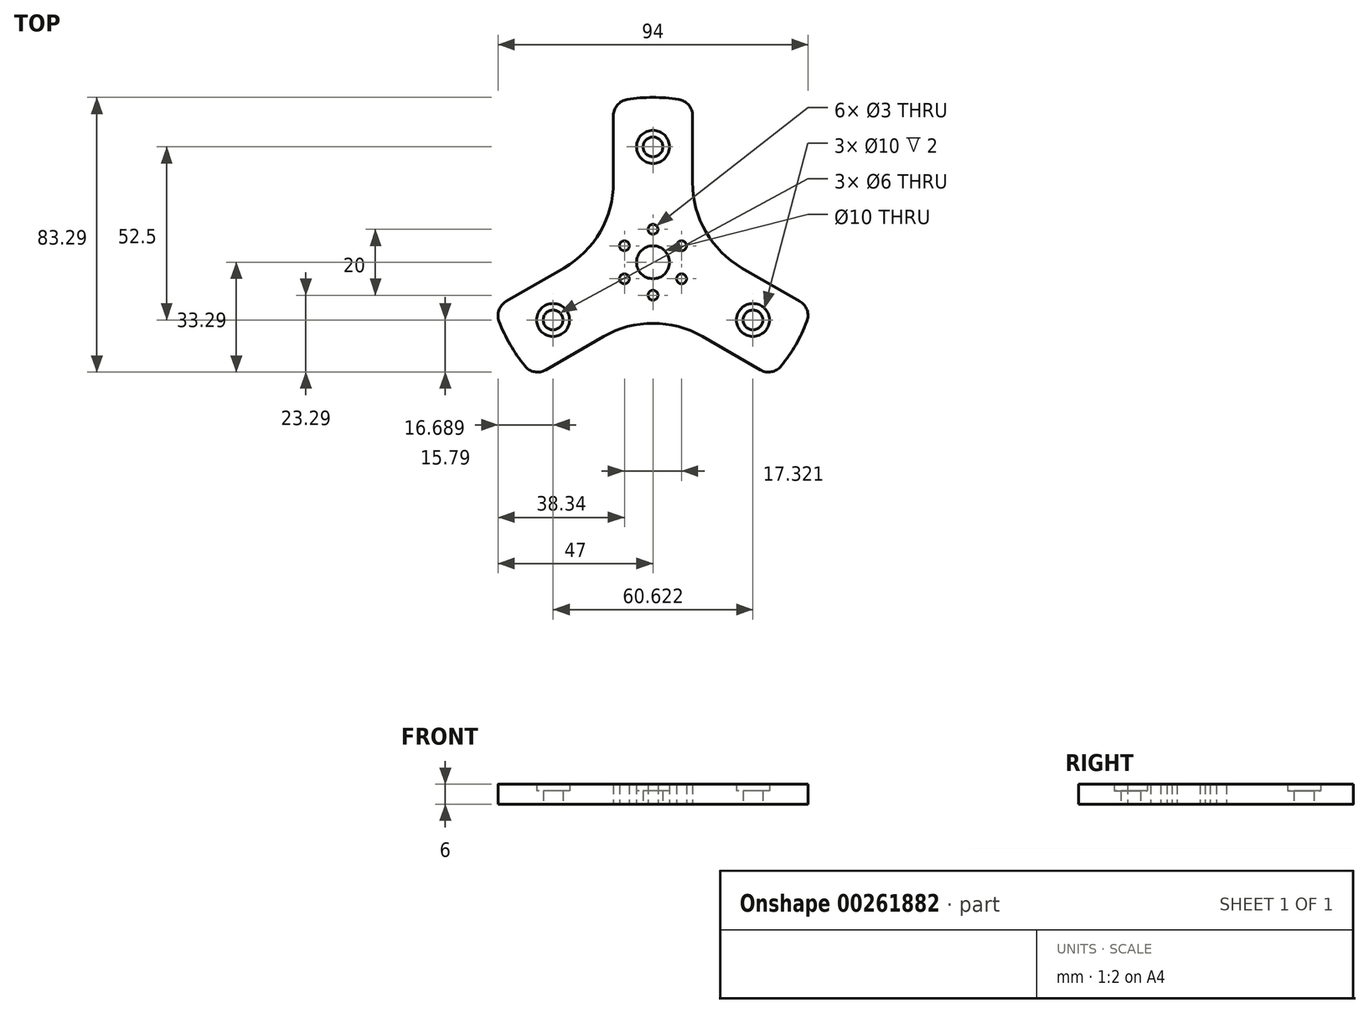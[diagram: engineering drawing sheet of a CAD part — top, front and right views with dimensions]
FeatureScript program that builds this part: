
annotation { "Feature Type Name" : "Feature", "Feature Type Description" : "" }
export const myFeature = defineFeature(function(context is Context, id is Id, definition is map)
    precondition{}
    {
        {
            var Q0;
            Q0=qCreatedBy(makeId("Top.planeOp"),FACE);
            var sketch = newSketch(context, id + "F0", { "sketchPlane" : qUnion([Q0])});
            skArc(sketch, "E0", {"start": v(-46.66, -17.96) * mm, "mid": v(-43.3, -25) * mm, "end": v(-38.89, -31.43) * mm});
            skLineSegment(sketch, "E1", {"start": v(0, 0) * mm, "end": v(-43.3, -25) * mm, "construction": true});
            skLineSegment(sketch, "E2", {"start": v(0, 0) * mm, "end": v(43.3, -25) * mm, "construction": true});
            skLineSegment(sketch, "E3", {"start": v(0, 0) * mm, "end": v(0, 50) * mm, "construction": true});
            skLineSegment(sketch, "E4.0", {"start": v(12, 24.25) * mm, "end": v(12, 44.45) * mm});
            skLineSegment(sketch, "E5.0", {"start": v(-12, 24.25) * mm, "end": v(-12, 44.45) * mm});
            skLineSegment(sketch, "E6.0", {"start": v(15, -22.52) * mm, "end": v(32.5, -32.62) * mm});
            skLineSegment(sketch, "E7.0", {"start": v(27, -1.73) * mm, "end": v(44.5, -11.83) * mm});
            skLineSegment(sketch, "E8.0", {"start": v(-27, -1.73) * mm, "end": v(-44.5, -11.83) * mm});
            skLineSegment(sketch, "E9.0", {"start": v(-15, -22.52) * mm, "end": v(-32.5, -32.62) * mm});
            skArc(sketch, "E10.trimOffspring", {"start": v(7.78, 49.4) * mm, "mid": v(0, 50) * mm, "end": v(-7.78, 49.4) * mm});
            skArc(sketch, "E11.trimOffspring", {"start": v(38.89, -31.43) * mm, "mid": v(43.3, -25) * mm, "end": v(46.66, -17.96) * mm});
            skPoint(sketch, "E12.visualSharp", {"position": v(-12, 48.54) * mm});
            skArc(sketch, "E12.filletArc", {"start": v(-7.78, 49.4) * mm, "mid": v(-10.8, 47.7) * mm, "end": v(-12, 44.45) * mm});
            skPoint(sketch, "E13.visualSharp", {"position": v(12, 48.54) * mm});
            skArc(sketch, "E13.filletArc", {"start": v(12, 44.45) * mm, "mid": v(10.8, 47.7) * mm, "end": v(7.78, 49.4) * mm});
            skPoint(sketch, "E14.visualSharp", {"position": v(48.04, -13.88) * mm});
            skArc(sketch, "E14.filletArc", {"start": v(46.66, -17.96) * mm, "mid": v(46.71, -14.5) * mm, "end": v(44.5, -11.83) * mm});
            skPoint(sketch, "E15.visualSharp", {"position": v(36.04, -34.66) * mm});
            skArc(sketch, "E15.filletArc", {"start": v(32.5, -32.62) * mm, "mid": v(35.91, -33.2) * mm, "end": v(38.89, -31.43) * mm});
            skPoint(sketch, "E16.visualSharp", {"position": v(-36.04, -34.66) * mm});
            skArc(sketch, "E16.filletArc", {"start": v(-38.89, -31.43) * mm, "mid": v(-35.91, -33.2) * mm, "end": v(-32.5, -32.62) * mm});
            skPoint(sketch, "E17.visualSharp", {"position": v(-48.04, -13.88) * mm});
            skArc(sketch, "E17.filletArc", {"start": v(-44.5, -11.83) * mm, "mid": v(-46.71, -14.5) * mm, "end": v(-46.66, -17.96) * mm});
            skPoint(sketch, "E18.visualSharp", {"position": v(-12, 6.93) * mm});
            skArc(sketch, "E18.filletArc", {"start": v(-27, -1.73) * mm, "mid": v(-16.02, 9.25) * mm, "end": v(-12, 24.25) * mm});
            skPoint(sketch, "E19.visualSharp", {"position": v(0, -13.86) * mm});
            skArc(sketch, "E19.filletArc", {"start": v(15, -22.52) * mm, "mid": v(0, -18.5) * mm, "end": v(-15, -22.52) * mm});
            skPoint(sketch, "E20.visualSharp", {"position": v(12, 6.93) * mm});
            skArc(sketch, "E20.filletArc", {"start": v(12, 24.25) * mm, "mid": v(16.02, 9.25) * mm, "end": v(27, -1.73) * mm});
            skCircle(sketch, "E21", {"center": v(0, 0) * mm, "radius": 35 * mm, "construction": true});
            skCircle(sketch, "E22", {"center": v(-30.31, -17.5) * mm, "radius": 5 * mm});
            skCircle(sketch, "E23", {"center": v(30.31, -17.5) * mm, "radius": 5 * mm});
            skCircle(sketch, "E24", {"center": v(0, 35) * mm, "radius": 5 * mm});
            skCircle(sketch, "E25", {"center": v(-30.31, -17.5) * mm, "radius": 3 * mm});
            skCircle(sketch, "E26", {"center": v(30.31, -17.5) * mm, "radius": 3 * mm});
            skCircle(sketch, "E27", {"center": v(0, 35) * mm, "radius": 3 * mm});
            skCircle(sketch, "E28", {"center": v(0, 0) * mm, "radius": 5 * mm});
            skCircle(sketch, "E29", {"center": v(0, 0) * mm, "radius": 10 * mm, "construction": true});
            skCircle(sketch, "E30", {"center": v(0, 10) * mm, "radius": 1.5 * mm});
            skCircle(sketch, "E31.1.0", {"center": v(-8.66, 5) * mm, "radius": 1.5 * mm});
            skCircle(sketch, "E31.2.0", {"center": v(-8.66, -5) * mm, "radius": 1.5 * mm});
            skCircle(sketch, "E31.3.0", {"center": v(0, -10) * mm, "radius": 1.5 * mm});
            skCircle(sketch, "E31.4.0", {"center": v(8.66, -5) * mm, "radius": 1.5 * mm});
            skCircle(sketch, "E31.5.0", {"center": v(8.66, 5) * mm, "radius": 1.5 * mm});
            skSolve(sketch);
        }
        {
            var Q0;
            Q0=makeQuery(id+"F0.imprint","IMPRINT",FACE,{"disambiguationData":[TD([[makeQuery(id+"F0.imprint","IMPRINT",EDGE,{"derivedFrom":sQuery(id+"F0.wireOp",EDGE,"E0")}),1.0]])]});
            extrude(context, id + "F1", {"entities" : qUnion([Q0]), "depth" : 6 * mm});
        }
        {
            var Q0;
            Q0=makeQuery(id+"F0.imprint","IMPRINT",FACE,{"disambiguationData":[TD([[makeQuery(id+"F0.imprint","IMPRINT",EDGE,{"derivedFrom":sQuery(id+"F0.wireOp",EDGE,"E22")}),1.0]])]});
            var Q1;
            Q1=makeQuery(id+"F0.imprint","IMPRINT",FACE,{"disambiguationData":[TD([[makeQuery(id+"F0.imprint","IMPRINT",EDGE,{"derivedFrom":sQuery(id+"F0.wireOp",EDGE,"E24")}),1.0]])]});
            var Q2;
            Q2=makeQuery(id+"F0.imprint","IMPRINT",FACE,{"disambiguationData":[TD([[makeQuery(id+"F0.imprint","IMPRINT",EDGE,{"derivedFrom":sQuery(id+"F0.wireOp",EDGE,"E23")}),1.0]])]});
            extrude(context, id + "F2", {"entities" : qUnion([Q0, Q1, Q2]), "operationType" : NewBodyOperationType.ADD, "depth" : 4 * mm});
        }
    });
